# Revit family: Air Source 280,000 BTU
name_source: partatom
category: Mechanical Equipment
revit_build: Autodesk Revit 2018 (Build: 20181015_0930(x64)
units: mm (PartAtom-declared; Revit-internal decimal feet)

## family parameters
Always vertical = Yes
Cut with Voids When Loaded = No
Part Type = Normal
Room Calculation Point = No
Round Connector Dimension = Use Diameter
Shared = No
Work Plane-Based = No

## types (1)
- 280,000 BTU
    440V-480V/3PH/60HZ MCA = 87.50
    440V-480V/3PH/60HZ MOCP = 90
    440V-480V/3PH/60HZ RLA = 70
    Air Volume (CFM) = 7,683
    BTUH Heating = 271,794
    Clearance Front = 36"
    Clearance Left = 24"
    Clearance Rear = 36"
    Clearance Right = 24"
    Compressor Type = Scroll
    Description = Air Source Heat Pump Water Heater
    Lbs.R513a = 28
    Manufacturer = Lochinvar
    SES BIM Studio # = 23 0649 01
    UNIT LENGTH = 34"
    UNIT WIDTH = 41 5/8"
    WATER CONN SIZE = 1 1/2"
    WEIGHT = 1,534

## geometry (parser evidence)
native form markers: Sweep x5
no freeform markers — native parametric forms only
